# Revit family: Water_Fountain-Haws_Combination_Unit_8320_8325
name_source: partatom
category: Plumbing Fixtures
revit_build: Autodesk Revit MEP 2013 (Build: 20130531_2115(x64)
units: mm (PartAtom-declared; Revit-internal decimal feet)

## types (1)
- Axion MSR - Combination Unit
    Assembly Code = D2010710
    Bowl = ABS Plastic - Haws Corporation - Green Powder Coating
    CW Connection = Yes
    CWFU = 1
    Cost Note = For Cost information please visit the Resource tab in the Product Page URL
    Description = Traditional eyewashes irrigate from the outside edge of the eye back toward the nose
    Eye/face wash head = 41 3/4"
    Flow = 20 GPM
    Full Height = 89 1/4"
    HW Connection = No
    HWFU = 1
    Keynote = 15410
    Lever Height = 65 3/8"
    Manufacturer = Haws Corporation 1455 Kleppe Lane Sparks, NV 89431
    Model = 8320-8325
    Product Documentation Link = http://www.hawsco.com
    Product Page URL = http://www.hawsco.com
    Pull Rod = Metal - Haws Corporation - High Polished Stainless Steel
    Sanitary Radius = 5/8"
    Series = AXION MSR™
    Shower Arm Overhang = 25"
    Shower Head = ABS Plastic - Haws Corporation - Green Powder Coating
    Supply Radius = 5/8"
    Tubing = Metal - Haws Corporation - Galvanized Steel
    Type Comments = Combination shower and eyewash features the medically acclaimed AXION MSR™ eye/face wash head assembly
    URL = http://www.hawsco.com
    Vent Connection = No
    WFU = 1
    Waste Connection = Yes

## geometry (parser evidence)
native form markers: Blend x38, Sweep x10
no freeform markers — native parametric forms only
